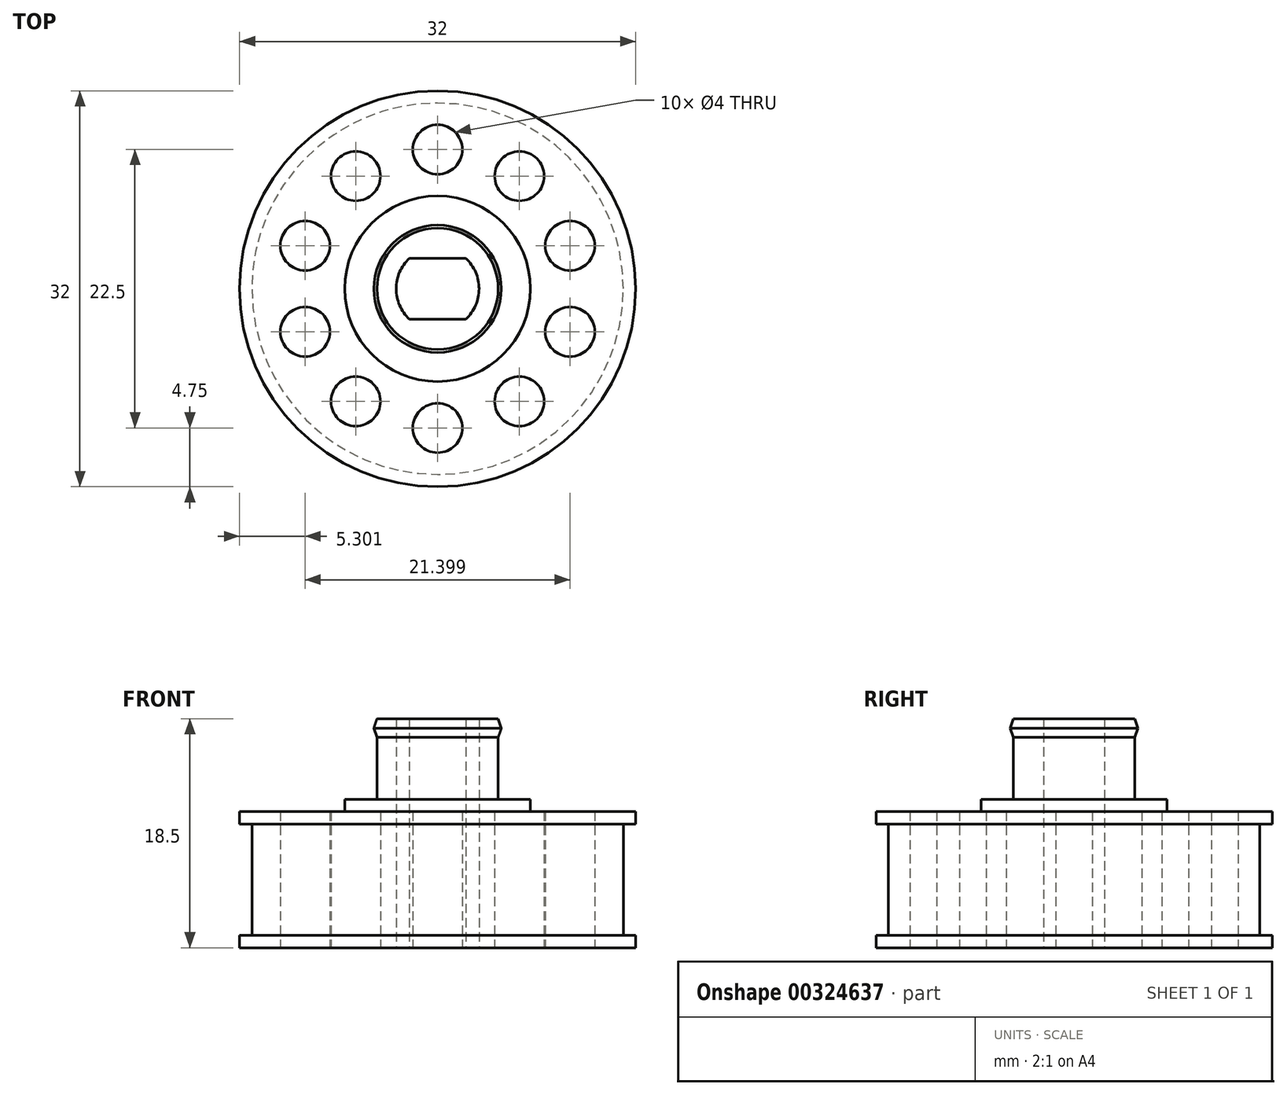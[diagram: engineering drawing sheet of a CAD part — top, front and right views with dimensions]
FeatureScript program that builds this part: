
annotation { "Feature Type Name" : "Feature", "Feature Type Description" : "" }
export const myFeature = defineFeature(function(context is Context, id is Id, definition is map)
    precondition{}
    {
        {
            assignVariable(context, id + "F0", {"name" : "e", "anyValue" : 6});
        }
        {
            assignVariable(context, id + "F1", {"name" : "h1", "anyValue" : 3});
        }
        {
            var Q0;
            Q0=qCreatedBy(makeId("Top.planeOp"),FACE);
            var sketch = newSketch(context, id + "F2", { "sketchPlane" : qUnion([Q0])});
            skCircle(sketch, "E0", {"center": v(0, 0) * mm, "radius": 15 * mm});
            skCircle(sketch, "E1", {"center": v(0, 0) * mm, "radius": 7.5 * mm});
            skCircle(sketch, "E2", {"center": v(0, 0) * mm, "radius": 4.9 * mm});
            skArc(sketch, "E3", {"start": v(-2.28, 2.45) * mm, "mid": v(-3.35, 0) * mm, "end": v(-2.28, -2.45) * mm});
            skLineSegment(sketch, "E4.bottom", {"start": v(2.28, -2.45) * mm, "end": v(-2.28, -2.45) * mm});
            skLineSegment(sketch, "E4.top", {"start": v(2.28, 2.45) * mm, "end": v(-2.28, 2.45) * mm});
            skArc(sketch, "E5.trimOffspring", {"start": v(2.28, -2.45) * mm, "mid": v(3.35, 0) * mm, "end": v(2.28, 2.45) * mm});
            skPoint(sketch, "E6.orphan", {"position": v(3.35, 2.45) * mm});
            skPoint(sketch, "E7.orphan", {"position": v(3.35, -2.45) * mm});
            skPoint(sketch, "E8.orphan", {"position": v(-3.35, -2.45) * mm});
            skPoint(sketch, "E9.orphan", {"position": v(-3.35, 2.45) * mm});
            skLineSegment(sketch, "E10", {"start": v(0, 7.5) * mm, "end": v(0, 15) * mm, "construction": true});
            skPoint(sketch, "E10.endSnap0", {"position": v(0, 2.45) * mm});
            skCircle(sketch, "E11", {"center": v(0, 11.25) * mm, "radius": 2 * mm});
            skCircle(sketch, "E12.1.0", {"center": v(-6.61, 9.1) * mm, "radius": 2 * mm});
            skCircle(sketch, "E12.2.0", {"center": v(-10.7, 3.48) * mm, "radius": 2 * mm});
            skCircle(sketch, "E12.3.0", {"center": v(-10.7, -3.48) * mm, "radius": 2 * mm});
            skCircle(sketch, "E12.4.0", {"center": v(-6.61, -9.1) * mm, "radius": 2 * mm});
            skCircle(sketch, "E12.5.0", {"center": v(0, -11.25) * mm, "radius": 2 * mm});
            skCircle(sketch, "E12.6.0", {"center": v(6.61, -9.1) * mm, "radius": 2 * mm});
            skCircle(sketch, "E12.7.0", {"center": v(10.7, -3.48) * mm, "radius": 2 * mm});
            skCircle(sketch, "E12.8.0", {"center": v(10.7, 3.48) * mm, "radius": 2 * mm});
            skCircle(sketch, "E12.9.0", {"center": v(6.61, 9.1) * mm, "radius": 2 * mm});
            skCircle(sketch, "E13", {"center": v(0, 0) * mm, "radius": 16 * mm});
            skSolve(sketch);
        }
        {
            var Q0;
            Q0=makeQuery(id+"F2.imprint","IMPRINT",FACE,{"disambiguationData":[TD([[makeQuery(id+"F2.imprint","IMPRINT",EDGE,{"derivedFrom":sQuery(id+"F2.wireOp",EDGE,"E0")}),1.0]])]});
            var Q1;
            Q1=makeQuery(id+"F2.imprint","IMPRINT",FACE,{"disambiguationData":[TD([[makeQuery(id+"F2.imprint","IMPRINT",EDGE,{"derivedFrom":sQuery(id+"F2.wireOp",EDGE,"E1")}),1.0]])]});
            var Q2;
            Q2=makeQuery(id+"F2.imprint","IMPRINT",FACE,{"disambiguationData":[TD([[makeQuery(id+"F2.imprint","IMPRINT",EDGE,{"derivedFrom":sQuery(id+"F2.wireOp",EDGE,"E2")}),1.0]])]});
            extrude(context, id + "F3", {"entities" : qUnion([Q0, Q1, Q2]), "depth" : 11 * mm});
        }
        {
            var Q0;
            Q0=makeQuery(id+"F2.imprint","IMPRINT",FACE,{"disambiguationData":[TD([[makeQuery(id+"F2.imprint","IMPRINT",EDGE,{"derivedFrom":sQuery(id+"F2.wireOp",EDGE,"E1")}),1.0]])]});
            var Q1;
            Q1=makeQuery(id+"F2.imprint","IMPRINT",FACE,{"disambiguationData":[TD([[makeQuery(id+"F2.imprint","IMPRINT",EDGE,{"derivedFrom":sQuery(id+"F2.wireOp",EDGE,"E2")}),1.0]])]});
            extrude(context, id + "F4", {"entities" : qUnion([Q0, Q1]), "operationType" : NewBodyOperationType.ADD, "depth" : (getVariable(context, 'e') + getVariable(context, 'h1')) * mm});
        }
        {
            var Q0;
            Q0=makeQuery(id+"F2.imprint","IMPRINT",FACE,{"disambiguationData":[TD([[makeQuery(id+"F2.imprint","IMPRINT",EDGE,{"derivedFrom":sQuery(id+"F2.wireOp",EDGE,"E2")}),1.0]])]});
            extrude(context, id + "F5", {"entities" : qUnion([Q0]), "operationType" : NewBodyOperationType.ADD, "depth" : 18.5 * mm});
        }
        {
            var Q0;
            Q0=qCreatedBy(makeId("Front.planeOp"),FACE);
            var sketch = newSketch(context, id + "F6", { "sketchPlane" : qUnion([Q0])});
            skLineSegment(sketch, "E14", {"start": v(0, 0) * mm, "end": v(0, 17.5) * mm, "construction": true});
            skLineSegment(sketch, "E15", {"start": v(-4.9, 6) * mm, "end": v(-4.9, 12.5) * mm});
            skLineSegment(sketch, "E16", {"start": v(4.9, 18.5) * mm, "end": v(4.9, 6) * mm});
            skLineSegment(sketch, "E17.bottom", {"start": v(4.9, 18.5) * mm, "end": v(5.15, 18.5) * mm, "construction": true});
            skLineSegment(sketch, "E17.top", {"start": v(4.9, 17) * mm, "end": v(5.15, 17) * mm, "construction": true});
            skLineSegment(sketch, "E17.left", {"start": v(4.9, 18.5) * mm, "end": v(4.9, 17) * mm, "construction": true});
            skLineSegment(sketch, "E17.right", {"start": v(5.15, 18.5) * mm, "end": v(5.15, 17) * mm, "construction": true});
            skPoint(sketch, "E18", {"position": v(5.15, 17.75) * mm});
            skLineSegment(sketch, "E19", {"start": v(4.9, 18.5) * mm, "end": v(5.15, 17.75) * mm});
            skLineSegment(sketch, "E20", {"start": v(5.15, 17.75) * mm, "end": v(4.9, 17) * mm});
            skLineSegment(sketch, "E21", {"start": v(4.9, 17) * mm, "end": v(4.9, 18.5) * mm});
            skSolve(sketch);
        }
        {
            var Q0;
            Q0=makeQuery(id+"F6.imprint","IMPRINT",FACE,{"disambiguationData":[TD([[makeQuery(id+"F6.imprint","IMPRINT",EDGE,{"derivedFrom":sQuery(id+"F6.wireOp",EDGE,"E19")}),-1.0]])]});
            var Q1;
            Q1=sQuery(id+"F6.wireOp",EDGE,"E14");
            revolve(context, id + "F7", {"operationType" : NewBodyOperationType.ADD, "entities" : qUnion([Q0]), "axis" : qUnion([Q1]), "revolveType" : RevolveType.FULL});
        }
        {
            var Q0;
            Q0=makeQuery(id+"F5.opExtrude","CAP_FACE",FACE,{"disambiguationData":[OSD([sQuery(id+"F2.wireOp",EDGE,"E2"),sQuery(id+"F2.wireOp",EDGE,"E3"),sQuery(id+"F2.wireOp",EDGE,"E4.bottom"),sQuery(id+"F2.wireOp",EDGE,"E4.top"),sQuery(id+"F2.wireOp",EDGE,"E5.trimOffspring")])],"isStart":false});
            cPlane(context, id + "F8", {"entities" : qUnion([Q0]), "cplaneType" : CPlaneType.OFFSET, "offset" : 0 * mm, "width" : 150 * mm, "height" : 150 * mm});
        }
        {
            var Q0;
            Q0=qCreatedBy(id+"F8.planeOp",FACE);
            var sketch = newSketch(context, id + "F9", { "sketchPlane" : qUnion([Q0])});
            skArc(sketch, "E22", {"start": v(-2.38, 2.7) * mm, "mid": v(-3.6, 0) * mm, "end": v(-2.38, -2.7) * mm});
            skLineSegment(sketch, "E23.bottom", {"start": v(-2.38, 2.7) * mm, "end": v(2.38, 2.7) * mm});
            skLineSegment(sketch, "E23.top", {"start": v(-2.38, -2.7) * mm, "end": v(2.38, -2.7) * mm});
            skPoint(sketch, "E24.orphan", {"position": v(4.18, 2.7) * mm});
            skPoint(sketch, "E25.orphan", {"position": v(3.52, -2.7) * mm});
            skArc(sketch, "E26.trimOffspring", {"start": v(2.38, -2.7) * mm, "mid": v(3.6, 0) * mm, "end": v(2.38, 2.7) * mm});
            skPoint(sketch, "E27.orphan", {"position": v(-4.18, -2.7) * mm});
            skPoint(sketch, "E28.orphan", {"position": v(-3.52, 2.7) * mm});
            skSolve(sketch);
        }
        {
            var Q0;
            Q0=qSketchRegion(id+"F2",true);
            extrude(context, id + "F10", {"entities" : qUnion([Q0]), "operationType" : NewBodyOperationType.ADD, "depth" : 1 * mm});
        }
        {
            var Q0;
            Q0=makeQuery(id+"F2.imprint","IMPRINT",FACE,{"disambiguationData":[TD([[makeQuery(id+"F2.imprint","IMPRINT",EDGE,{"derivedFrom":sQuery(id+"F2.wireOp",EDGE,"E0")}),1.0]])]});
            var Q1;
            Q1=makeQuery(id+"F10.opExtrude","CAP_FACE",FACE,{"disambiguationData":[OSD([sQuery(id+"F2.wireOp",EDGE,"E0"),sQuery(id+"F2.wireOp",EDGE,"E13")])],"isStart":false});
            extrude(context, id + "F11", {"entities" : qUnion([Q0, Q1]), "operationType" : NewBodyOperationType.ADD, "depth" : 10 * mm, "hasSecondDirection" : true, "secondDirectionOppositeDirection" : false, "secondDirectionDepth" : 9 * mm});
        }
        {
            var Q0;
            Q0=makeQuery(id+"F2.imprint","IMPRINT",FACE,{"disambiguationData":[TD([[makeQuery(id+"F2.imprint","IMPRINT",EDGE,{"derivedFrom":sQuery(id+"F2.wireOp",EDGE,"E1")}),1.0]])]});
            extrude(context, id + "F12", {"entities" : qUnion([Q0]), "operationType" : NewBodyOperationType.ADD, "depth" : 12 * mm});
        }
    });
